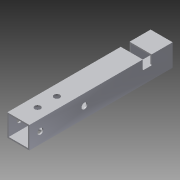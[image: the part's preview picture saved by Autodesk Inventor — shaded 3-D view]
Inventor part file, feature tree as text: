
AUTODESK INVENTOR PART (.ipt)
format: ipt  version: 2013 (Build 170138000, 138)  size: 113,664 bytes
history: native  units: in
note: dims shown in document units (in); Inventor stores cm internally (conversion verified against a paired STEP export)
features: reference x5, extrude x4, sketch x4
ambient origin geometry x8: Origin, YZ Plane, XZ Plane, XY Plane, X Axis, Y Axis, Z Axis, Center Point
bodies: Solid1 (feature_tree)
feature tree (13):
  extrude  "Extrusion1"  Depth=1.0in
  extrude  "Extrusion2"  Depth=6.5in TaperAngle=0.0deg
  extrude  "Extrusion3"  Depth=1.0in TaperAngle=0.0deg
  extrude  "Extrusion4"  [1 undecoded]
  sketch  "Sketch1"  dims[d0=1.0in d1=1.0in]
  sketch  "Sketch2"  dims[d2=0.0625in d3=6.5in d4=0.0in]
  reference  "Reference1"
  sketch  "Sketch3"  dims[d5=1.0in d6=0.0in d7=1.0in d8=0.0in]
  reference  "Reference2"
  reference  "Reference3"
  sketch  "Sketch4"  dims[d9=1.0in d10=0.0in]
  reference  "Reference4"
  reference  "Reference5"
note: 1 required parameter value undecoded (feature->parameter linkage not recoverable at this tier; creation-order binding heuristic only, values carry confidence <= 0.55)
